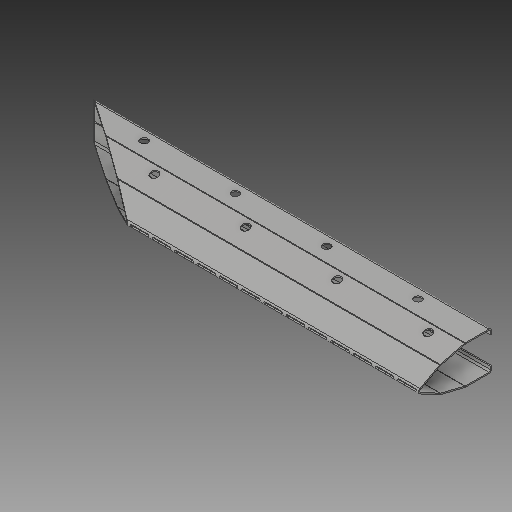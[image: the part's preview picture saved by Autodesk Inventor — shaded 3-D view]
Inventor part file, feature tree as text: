
AUTODESK INVENTOR PART (.ipt)
format: ipt  version: 2018 (Build 220112000, 112)  size: 808,448 bytes
history: native  units: mm
features: reference x24, other x20, sketch x14, sheet_metal_op x13, plane x9, projected_geometry x7, extrude x4
ambient origin geometry x8: Origin, YZ Plane, XZ Plane, XY Plane, X Axis, Y Axis, Z Axis, Center Point
bodies: Solid1 (feature_tree)
feature tree (91):
  plane  "Work Plane1"
  sheet_metal_op  "Face1"
  plane  "Work Plane2"
  sheet_metal_op  "Face2"
  plane  "Work Plane3"
  sheet_metal_op  "Face3"
  plane  "Work Plane4"
  sheet_metal_op  "Face4"
  plane  "Work Plane5"
  sheet_metal_op  "Face5"
  plane  "Work Plane6"
  sheet_metal_op  "Face6"
  plane  "Work Plane7"
  sheet_metal_op  "Face7"
  other  "midtplan"
  extrude  "Extrusion3"  Depth=5.0mm
  extrude  "hulsæt til stifter"  Depth=2.0mm
  plane  "Work Plane11"
  sketch  "Sketch13"  dims[d13=2.0mm]
  plane  "Work Plane12"
  extrude  "balusterhul"  Depth=5.0mm
  extrude  "balusterhul skråkompensering"  Depth=4.0mm
  sketch  "Sketch1"  dims[d0=4.0mm d1=5.0mm]
  reference  "Reference1"
  reference  "Reference2"
  reference  "Reference3"
  reference  "Reference4"
  other  "Plate1"
  sketch  "Sketch2"  dims[d2=4.0mm d3=2.0mm]
  reference  "Reference5"
  reference  "Reference6"
  reference  "Reference7"
  reference  "Reference8"
  other  "Plate2"
  sheet_metal_op  "Bend1"
  sketch  "Sketch3"  dims[d4=8.0mm d5=5.0mm]
  reference  "Reference9"
  reference  "Reference10"
  reference  "Reference11"
  other  "Plate3"
  sheet_metal_op  "Bend2"
  sketch  "Sketch4"  dims[d6=5.0mm d7=4.0mm]
  reference  "Reference12"
  reference  "Reference13"
  reference  "Reference14"
  reference  "Reference15"
  other  "Plate4"
  sheet_metal_op  "Bend3"
  sketch  "Sketch5"  dims[d8=2.0mm]
  reference  "Reference16"
  reference  "Reference17"
  reference  "Reference18"
  other  "Plate5"
  sheet_metal_op  "Bend4"
  sketch  "Sketch6"  dims[d9=8.0mm]
  reference  "Reference19"
  reference  "Reference20"
  reference  "Reference21"
  other  "Plate6"
  sheet_metal_op  "Bend5"
  sketch  "Sketch7"  dims[d10=5.0mm]
  reference  "Reference22"
  reference  "Reference23"
  other  "Plate7"
  sheet_metal_op  "Bend6"
  sketch  "Sketch8"  dims[d11=5.0mm]
  reference  "Reference24"
  projected_geometry  "Projected Loop1"
  other  "huller til stifter"
  projected_geometry  "Projected Loop3"
  sketch  "Sketch12"  dims[d12=4.0mm]
  projected_geometry  "Projected Loop4"
  sketch  "Sketch14"  dims[d14=8.0mm]
  sketch  "Sketch15"  dims[d15=5.0mm]
  projected_geometry  "Projected Loop5"
  projected_geometry  "Projected Loop6"
  sketch  "Sketch16"  dims[d16=5.0mm]
  projected_geometry  "Projected Loop7"
  projected_geometry  "Projected Loop8"
  sketch  "Sketch17"  dims[d17=4.0mm d18=2.0mm d19=8.0mm d20=5.0mm d21=5.0mm d22=4.0mm d23=2.0mm d24=8.0mm d25=5.0mm d26=5.0mm d27=4.0mm d28=2.0mm d29=8.0mm d30=5.0mm d31=4.0mm d32=0.0mm d33=3.0mm d39=250.0mm d41=33.7mm d42=33.7mm d43=60.0mm d44=60.0mm d45=16.85mm d46=65.0mm d47=60.0mm d48=10.0mm d49=0.0mm d69=10.0mm d70=0.0mm d73=96.672mm d75=5.986479mm d76=180.0mm d77=26.6mm d78=25.8mm d79=40.0mm d81=302.737mm d82=10.0mm d84=10.0mm d86=90.0deg d87=113.655385mm d88=56.827692mm d89=90.0deg d90=49.0mm d91=100.0mm d92=0.0mm d95=100.0mm d96=0.0mm d97=2.728615mm d99=1.364307mm d100=90.0mm d101=30.0mm d102=30.0mm d103=342.765mm d104=342.765mm d105=30.0mm d106=342.765mm d107=10.0mm d108=4.0mm d109=0.0mm d110=8.0mm d111=6.0mm d112=61.6mm d113=140.0mm d115=73.92mm d116=10.0mm d118=10.0mm d120=4.0mm d121=0.0mm]
  other  "Cut1"
  other  "plantehuller"
  other  "bukkeperforering"
  parser-record x3  (decoder bookkeeping rows leaked as tree rows — omitted from the tree; the rows remain in map.json)
  other  "modul bund.iam"
  other  "model:1"
  other  "Definition1"
  other  "modul.iam"
  other  "modul top.iam"
note: 3 file-system paths scrubbed to <path> (originals preserved in map.json)
